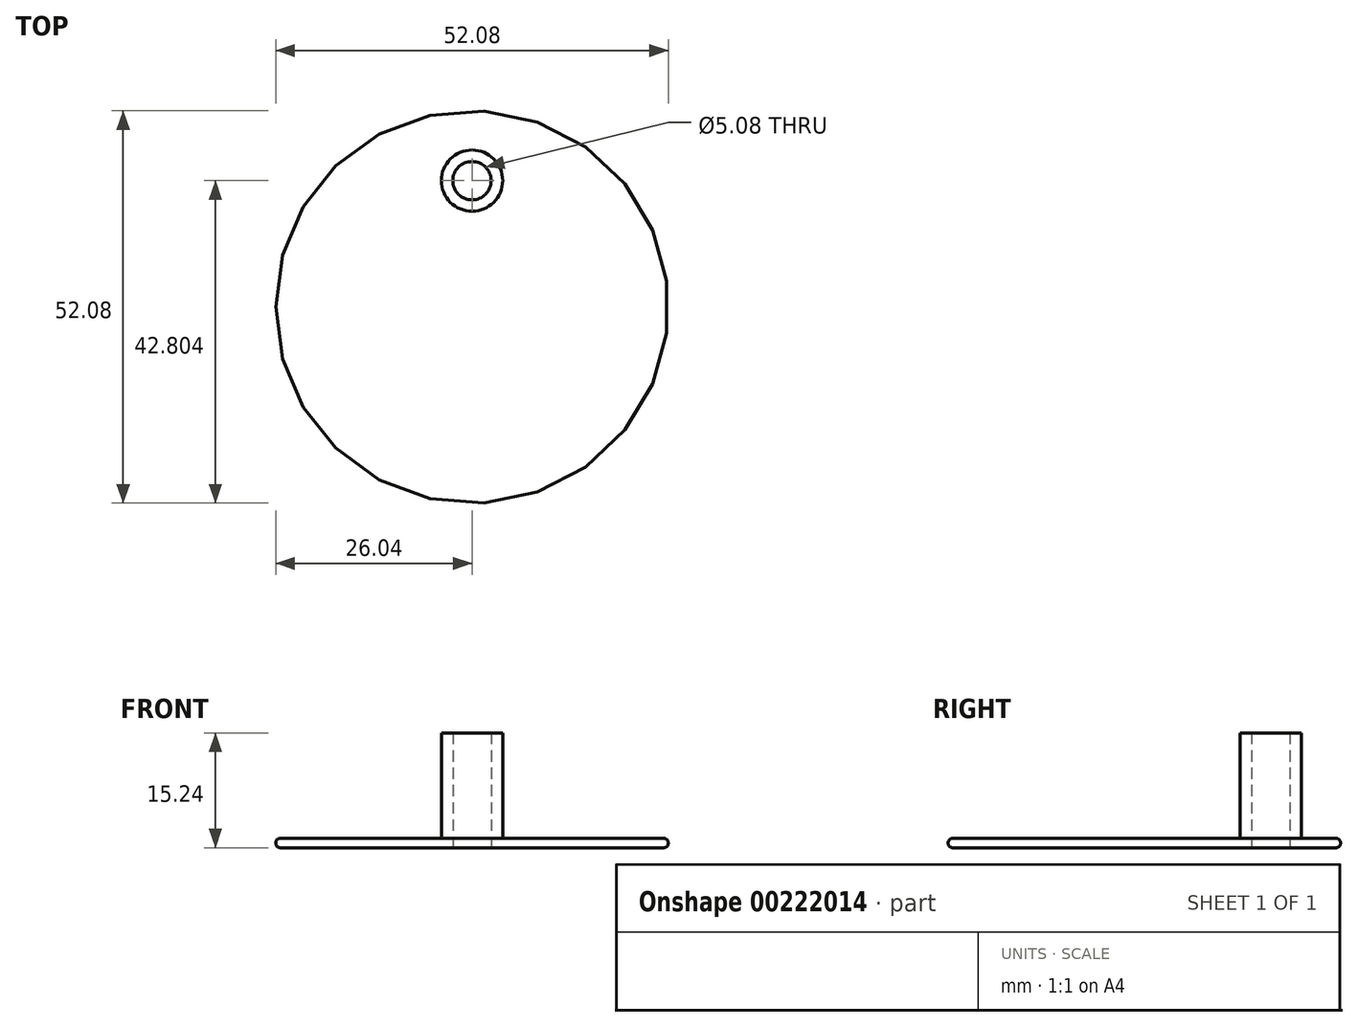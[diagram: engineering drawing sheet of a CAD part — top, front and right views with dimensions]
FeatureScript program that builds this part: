
annotation { "Feature Type Name" : "Feature", "Feature Type Description" : "" }
export const myFeature = defineFeature(function(context is Context, id is Id, definition is map)
    precondition{}
    {
        {
            var Q0;
            Q0=qCreatedBy(makeId("Front.planeOp"),FACE);
            var sketch = newSketch(context, id + "F0", { "sketchPlane" : qUnion([Q0])});
            skLineSegment(sketch, "E0", {"start": v(25.4, 0) * mm, "end": v(0, 0) * mm});
            skLineSegment(sketch, "E1", {"start": v(0, 0) * mm, "end": v(0, 1.27) * mm});
            skLineSegment(sketch, "E2", {"start": v(0, 1.27) * mm, "end": v(25.4, 1.27) * mm});
            skArc(sketch, "E3", {"start": v(25.4, 0) * mm, "mid": v(26.04, 0.64) * mm, "end": v(25.4, 1.27) * mm});
            skSolve(sketch);
        }
        {
            var Q0;
            Q0=makeQuery(id+"F0.imprint","IMPRINT",FACE,{"disambiguationData":[TD([[makeQuery(id+"F0.imprint","IMPRINT",EDGE,{"derivedFrom":sQuery(id+"F0.wireOp",EDGE,"E0")}),-1.0]])]});
            var Q1;
            Q1=sQuery(id+"F0.wireOp",EDGE,"E1");
            revolve(context, id + "F1", {"entities" : qUnion([Q0]), "axis" : qUnion([Q1]), "revolveType" : RevolveType.FULL});
        }
        {
            var Q0;
            Q0=qCreatedBy(makeId("Top.planeOp"),FACE);
            var sketch = newSketch(context, id + "F2", { "sketchPlane" : qUnion([Q0])});
            skCircle(sketch, "E4", {"center": v(0, 16.76) * mm, "radius": 4.06 * mm});
            skCircle(sketch, "E5", {"center": v(0, 16.76) * mm, "radius": 2.54 * mm});
            skSolve(sketch);
        }
        {
            var Q0;
            Q0=qSketchRegion(id+"F2",true);
            extrude(context, id + "F3", {"entities" : qUnion([Q0]), "operationType" : NewBodyOperationType.ADD, "depth" : 15.24 * mm});
        }
        {
            var Q0;
            Q0=qCreatedBy(makeId("Top.planeOp"),FACE);
            var sketch = newSketch(context, id + "F4", { "sketchPlane" : qUnion([Q0])});
            skCircle(sketch, "E6", {"center": v(0, 16.76) * mm, "radius": 2.54 * mm});
            skSolve(sketch);
        }
        {
            var Q0;
            Q0=qSketchRegion(id+"F4",true);
            extrude(context, id + "F5", {"entities" : qUnion([Q0]), "operationType" : NewBodyOperationType.REMOVE, "depth" : 12.7 * mm, "hasSecondDirection" : true, "secondDirectionOppositeDirection" : true, "secondDirectionDepth" : 5.33 * mm});
        }
    });
